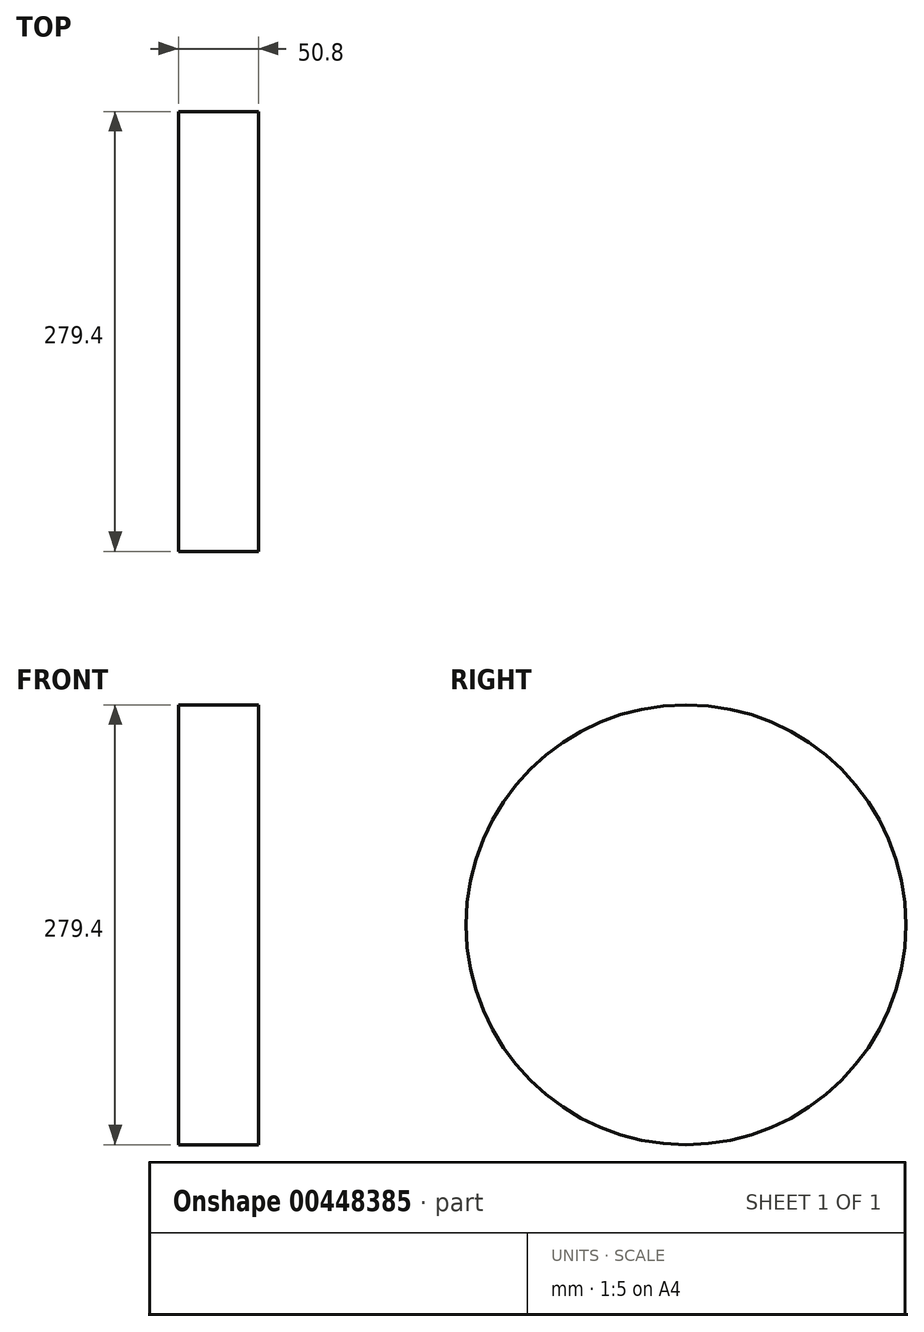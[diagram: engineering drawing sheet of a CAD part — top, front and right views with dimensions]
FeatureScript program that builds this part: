
annotation { "Feature Type Name" : "Feature", "Feature Type Description" : "" }
export const myFeature = defineFeature(function(context is Context, id is Id, definition is map)
    precondition{}
    {
        {
            var Q0;
            Q0=qCreatedBy(makeId("Right.planeOp"),FACE);
            var sketch = newSketch(context, id + "F0", { "sketchPlane" : qUnion([Q0])});
            skCircle(sketch, "E0", {"center": v(-16.9, 0) * mm, "radius": 139.7 * mm});
            skSolve(sketch);
        }
        {
            var Q0;
            Q0=makeQuery(id+"F0.imprint","IMPRINT",FACE,{"disambiguationData":[TD([[makeQuery(id+"F0.imprint","IMPRINT",EDGE,{"derivedFrom":sQuery(id+"F0.wireOp",EDGE,"E0")}),1.0]])]});
            extrude(context, id + "F1", {"entities" : qUnion([Q0]), "depth" : 50.8 * mm});
        }
    });
